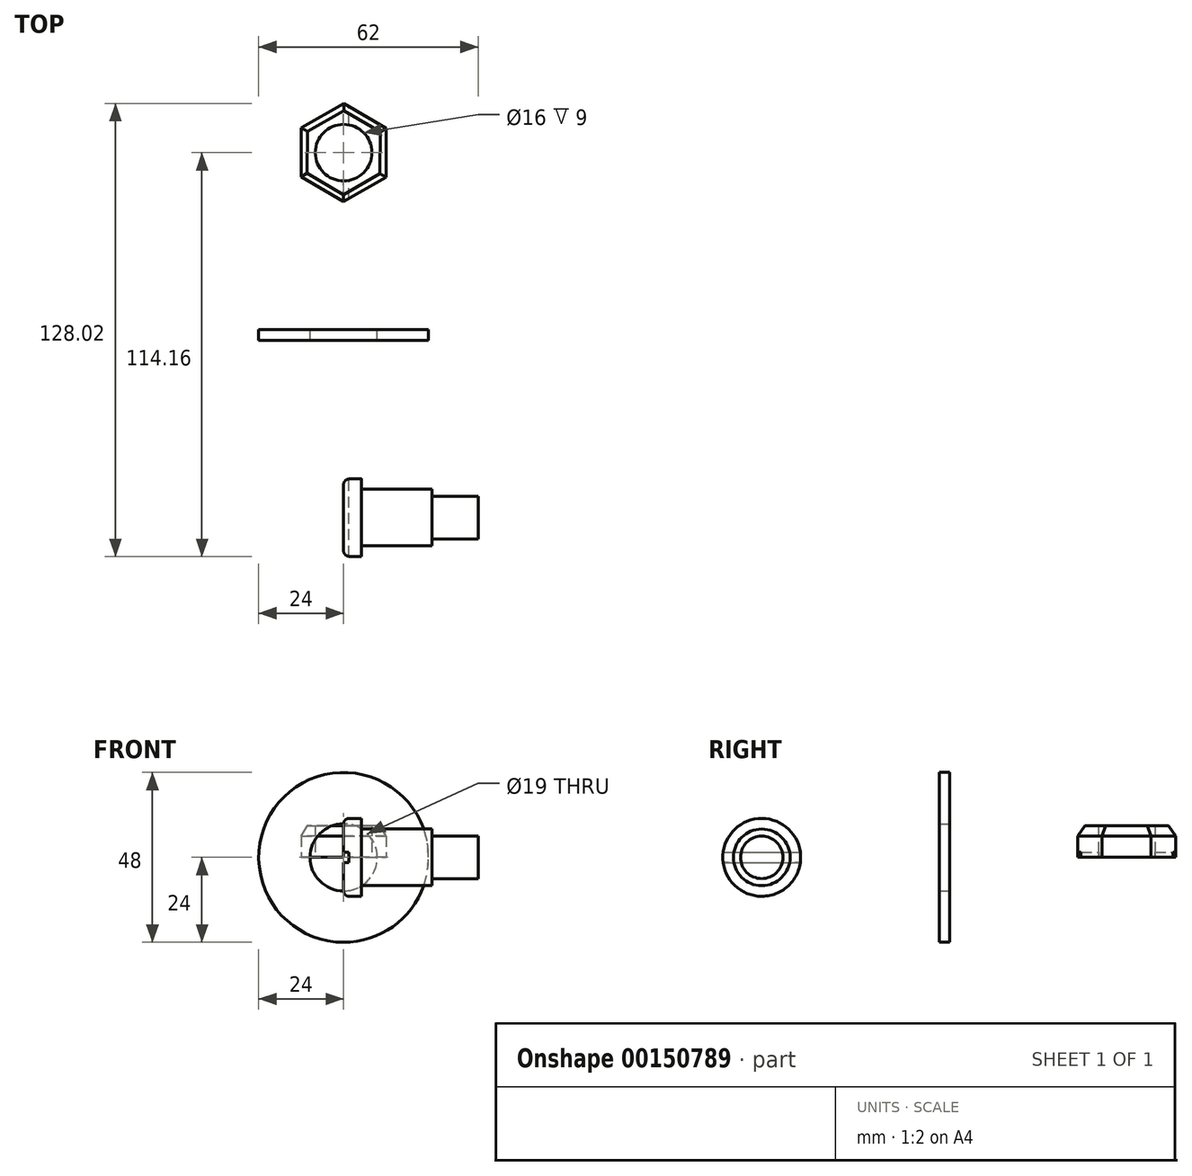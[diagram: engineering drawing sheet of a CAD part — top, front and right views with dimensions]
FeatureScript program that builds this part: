
annotation { "Feature Type Name" : "Feature", "Feature Type Description" : "" }
export const myFeature = defineFeature(function(context is Context, id is Id, definition is map)
    precondition{}
    {
        {
            var Q0;
            Q0=qCreatedBy(makeId("Front.planeOp"),FACE);
            var sketch = newSketch(context, id + "F0", { "sketchPlane" : qUnion([Q0])});
            skCircle(sketch, "E0", {"center": v(0, 0) * mm, "radius": 24 * mm});
            skCircle(sketch, "E1", {"center": v(0, 0) * mm, "radius": 9.5 * mm});
            skSolve(sketch);
        }
        {
            var Q0;
            Q0=qSketchRegion(id+"F0",true);
            extrude(context, id + "F1", {"entities" : qUnion([Q0]), "depth" : 3 * mm});
        }
        {
            var Q0;
            Q0=qCreatedBy(makeId("Top.planeOp"),FACE);
            var sketch = newSketch(context, id + "F2", { "sketchPlane" : qUnion([Q0])});
            skLineSegment(sketch, "E2", {"start": v(0, 0) * mm, "end": v(0, 50) * mm, "construction": true});
            skCircle(sketch, "E3.cCircle", {"center": v(0, 50) * mm, "radius": 12 * mm, "construction": true});
            skLineSegment(sketch, "E3.0", {"start": v(-11.96, 57) * mm, "end": v(0.07, 63.86) * mm});
            skLineSegment(sketch, "E3.1", {"start": v(0.07, 63.86) * mm, "end": v(12.04, 56.86) * mm});
            skLineSegment(sketch, "E3.2", {"start": v(12.04, 56.86) * mm, "end": v(11.96, 43) * mm});
            skLineSegment(sketch, "E3.3", {"start": v(11.96, 43) * mm, "end": v(-0.07, 36.14) * mm});
            skLineSegment(sketch, "E3.4", {"start": v(-0.07, 36.14) * mm, "end": v(-12.04, 43.14) * mm});
            skLineSegment(sketch, "E3.5", {"start": v(-12.04, 43.14) * mm, "end": v(-11.96, 57) * mm});
            skPoint(sketch, "E3.0.midPoint", {"position": v(-5.94, 60.42) * mm});
            skCircle(sketch, "E4", {"center": v(0, 50) * mm, "radius": 8 * mm});
            skSolve(sketch);
        }
        {
            var Q0;
            Q0=qSketchRegion(id+"F2",true);
            extrude(context, id + "F3", {"entities" : qUnion([Q0]), "depth" : 9 * mm});
        }
        {
            var Q0;
            Q0=makeQuery(id+"F3.opExtrude","CAP_EDGE",EDGE,{"disambiguationData":[OSD([sQuery(id+"F2.wireOp",EDGE,"E3.2")])],"isStart":false});
            var Q1;
            Q1=makeQuery(id+"F3.opExtrude","CAP_EDGE",EDGE,{"disambiguationData":[OSD([sQuery(id+"F2.wireOp",EDGE,"E3.3")])],"isStart":false});
            var Q2;
            Q2=makeQuery(id+"F3.opExtrude","CAP_EDGE",EDGE,{"disambiguationData":[OSD([sQuery(id+"F2.wireOp",EDGE,"E3.4")])],"isStart":false});
            var Q3;
            Q3=makeQuery(id+"F3.opExtrude","CAP_EDGE",EDGE,{"disambiguationData":[OSD([sQuery(id+"F2.wireOp",EDGE,"E3.1")])],"isStart":false});
            var Q4;
            Q4=makeQuery(id+"F3.opExtrude","CAP_EDGE",EDGE,{"disambiguationData":[OSD([sQuery(id+"F2.wireOp",EDGE,"E3.0")])],"isStart":false});
            var Q5;
            Q5=makeQuery(id+"F3.opExtrude","CAP_EDGE",EDGE,{"disambiguationData":[OSD([sQuery(id+"F2.wireOp",EDGE,"E3.5")])],"isStart":false});
            chamfer(context, id + "F4", {"entities" : qUnion([Q0, Q1, Q2, Q3, Q4, Q5]), "chamferType" : ChamferType.OFFSET_ANGLE, "width" : 3 * mm, "oppositeDirection" : false, "angle" : 30 * degree, "tangentPropagation" : true});
        }
        {
            var Q0;
            Q0=qCreatedBy(makeId("Right.planeOp"),FACE);
            var sketch = newSketch(context, id + "F5", { "sketchPlane" : qUnion([Q0])});
            skLineSegment(sketch, "E5", {"start": v(0, 0) * mm, "end": v(-53.16, 0) * mm, "construction": true});
            skCircle(sketch, "E6", {"center": v(-53.16, 0) * mm, "radius": 11 * mm});
            skSolve(sketch);
        }
        {
            var Q0;
            Q0=qSketchRegion(id+"F5",true);
            extrude(context, id + "F6", {"entities" : qUnion([Q0]), "depth" : 5 * mm});
        }
        {
            var Q0;
            Q0=makeQuery(id+"F6.opExtrude","CAP_FACE",FACE,{"disambiguationData":[OSD([sQuery(id+"F5.wireOp",EDGE,"E6")])],"isStart":false});
            var sketch = newSketch(context, id + "F7", { "sketchPlane" : qUnion([Q0])});
            skCircle(sketch, "E7", {"center": v(-53.16, 0) * mm, "radius": 8 * mm});
            skSolve(sketch);
        }
        {
            var Q0;
            Q0=qSketchRegion(id+"F7",true);
            extrude(context, id + "F8", {"entities" : qUnion([Q0]), "operationType" : NewBodyOperationType.ADD, "depth" : 20 * mm});
        }
        {
            var Q0;
            Q0=makeQuery(id+"F8.opExtrude","CAP_FACE",FACE,{"disambiguationData":[OSD([sQuery(id+"F7.wireOp",EDGE,"E7")])],"isStart":false});
            var sketch = newSketch(context, id + "F9", { "sketchPlane" : qUnion([Q0])});
            skCircle(sketch, "E8", {"center": v(-53.16, 0) * mm, "radius": 6 * mm});
            skSolve(sketch);
        }
        {
            var Q0;
            Q0=qSketchRegion(id+"F9",true);
            extrude(context, id + "F10", {"entities" : qUnion([Q0]), "operationType" : NewBodyOperationType.ADD, "depth" : 13 * mm});
        }
        {
            var Q0;
            Q0=sQuery(id+"F5.wireOp",VERTEX,"E5.end");
            var Q1;
            Q1=qCreatedBy(makeId("Front.planeOp"),FACE);
            cPlane(context, id + "F11", {"entities" : qUnion([Q0, Q1]), "cplaneType" : CPlaneType.PLANE_POINT, "offset" : 25 * mm, "width" : 150 * mm, "height" : 150 * mm});
        }
        {
            var Q0;
            Q0=qCreatedBy(id+"F11.planeOp",FACE);
            var sketch = newSketch(context, id + "F12", { "sketchPlane" : qUnion([Q0])});
            skLineSegment(sketch, "E9", {"start": v(0, 1.5) * mm, "end": v(1.5, 1.5) * mm});
            skLineSegment(sketch, "E10", {"start": v(1.5, 1.5) * mm, "end": v(1.5, -1.5) * mm});
            skLineSegment(sketch, "E11", {"start": v(1.5, -1.5) * mm, "end": v(0, -1.5) * mm});
            skLineSegment(sketch, "E12", {"start": v(0, -1.5) * mm, "end": v(0, 0) * mm});
            skLineSegment(sketch, "E13", {"start": v(0, 1.5) * mm, "end": v(0, -1.5) * mm});
            skSolve(sketch);
        }
        {
            var Q0;
            Q0=qSketchRegion(id+"F12",true);
            extrude(context, id + "F13", {"entities" : qUnion([Q0]), "operationType" : NewBodyOperationType.REMOVE, "endBound" : BoundingType.THROUGH_ALL, "depth" : 25 * mm, "hasSecondDirection" : true, "secondDirectionBound" : SecondDirectionBoundingType.THROUGH_ALL, "secondDirectionOppositeDirection" : true, "secondDirectionDepth" : 25 * mm});
        }
        {
            var Q0;
            {var subQ0=sQuery(id+"F5.wireOp",EDGE,"E6");Q0=makeQuery(id+"F13.boolean.opBoolean","SPLIT",EDGE,{"disambiguationData":[TD([makeQuery(id+"F13.opExtrude","SWEPT_FACE",FACE,{"disambiguationData":[OSD([sQuery(id+"F12.wireOp",EDGE,"E9")])]})])],"derivedFrom":makeQuery(id+"F6.opExtrude","CAP_EDGE",EDGE,{"disambiguationData":[OSD([subQ0])],"isStart":true})});}
            var Q1;
            {var subQ0=sQuery(id+"F5.wireOp",EDGE,"E6");Q1=makeQuery(id+"F13.boolean.opBoolean","SPLIT",EDGE,{"disambiguationData":[TD([makeQuery(id+"F13.opExtrude","SWEPT_FACE",FACE,{"disambiguationData":[OSD([sQuery(id+"F12.wireOp",EDGE,"E11")])]})])],"derivedFrom":makeQuery(id+"F6.opExtrude","CAP_EDGE",EDGE,{"disambiguationData":[OSD([subQ0])],"isStart":true})});}
            fillet(context, id + "F14", {"entities" : qUnion([Q0, Q1]), "radius" : 1.5 * mm, "tangentPropagation" : true, "allowEdgeOverflow" : false});
        }
    });
